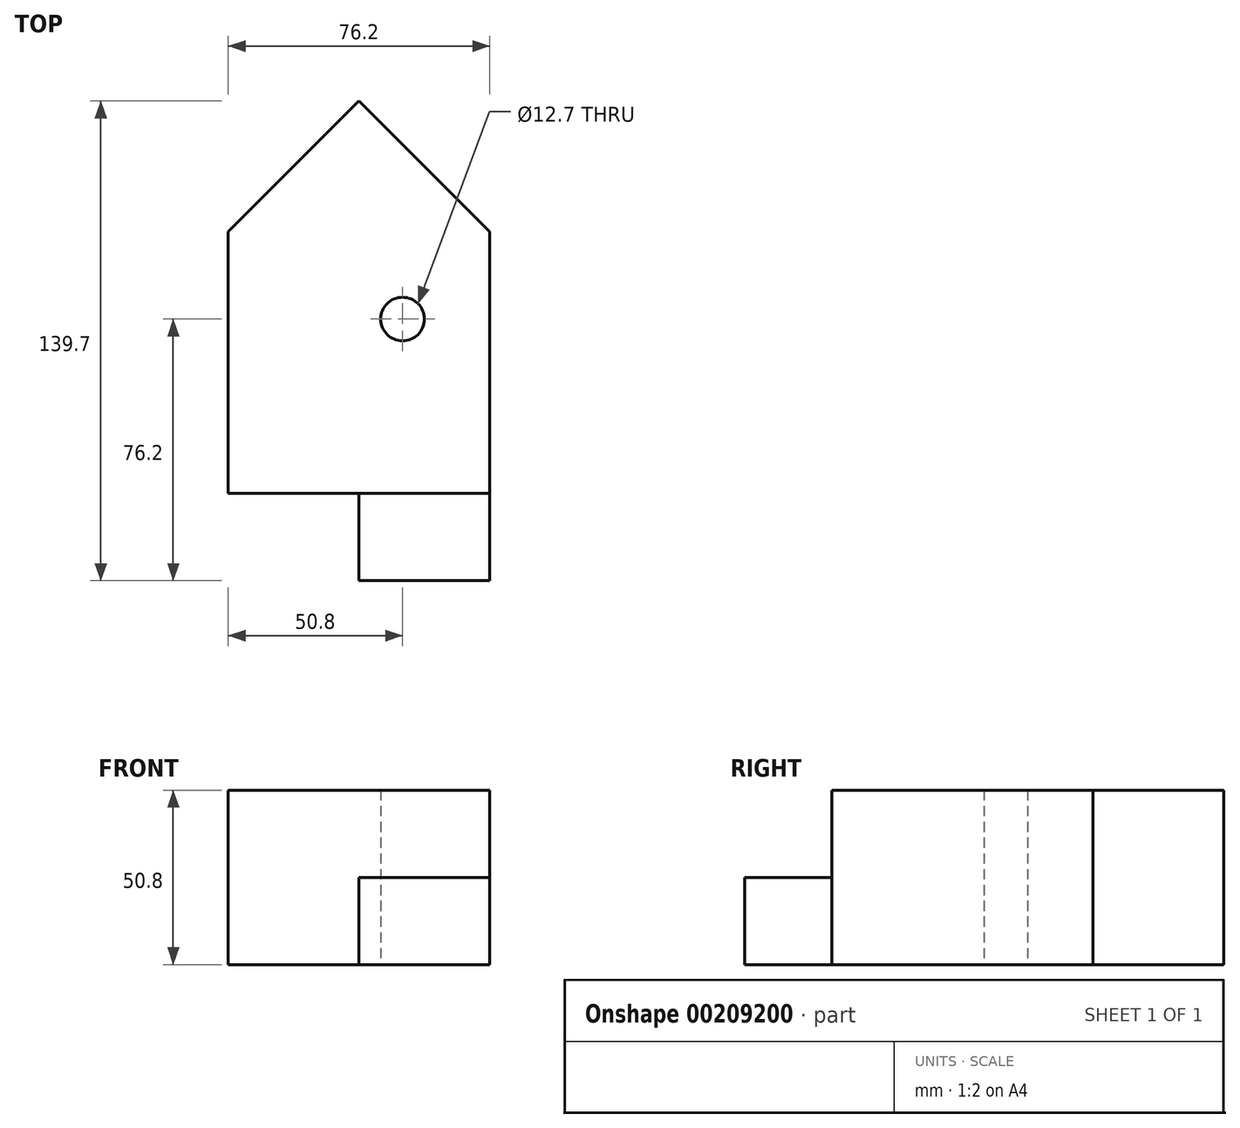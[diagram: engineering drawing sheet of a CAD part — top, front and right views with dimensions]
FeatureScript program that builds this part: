
annotation { "Feature Type Name" : "Feature", "Feature Type Description" : "" }
export const myFeature = defineFeature(function(context is Context, id is Id, definition is map)
    precondition{}
    {
        {
            var Q0;
            Q0=qCreatedBy(makeId("Top.planeOp"),FACE);
            var sketch = newSketch(context, id + "F0", { "sketchPlane" : qUnion([Q0])});
            skLineSegment(sketch, "E0.bottom", {"start": v(0, 0) * mm, "end": v(76.2, 0) * mm});
            skLineSegment(sketch, "E0.top", {"start": v(0, 76.2) * mm, "end": v(76.2, 76.2) * mm});
            skLineSegment(sketch, "E0.left", {"start": v(0, 0) * mm, "end": v(0, 76.2) * mm});
            skLineSegment(sketch, "E0.right", {"start": v(76.2, 0) * mm, "end": v(76.2, 76.2) * mm});
            skLineSegment(sketch, "E1", {"start": v(0, 76.2) * mm, "end": v(38.1, 114.3) * mm});
            skPoint(sketch, "E1.endSnap0", {"position": v(38.1, 76.2) * mm});
            skLineSegment(sketch, "E2", {"start": v(38.1, 114.3) * mm, "end": v(76.2, 76.2) * mm});
            skSolve(sketch);
        }
        {
            var Q0;
            Q0 = qSketchRegion(id + "F0", true);
            extrude(context, id + "F1", {"entities" : qUnion([Q0]), "depth" : 50.8 * mm});
        }
        {
            var Q0;
            Q0=makeQuery(id+"F1.opExtrude","CAP_FACE",FACE,{"disambiguationData":[OSD([sQuery(id+"F0.wireOp",EDGE,"E0.bottom"),sQuery(id+"F0.wireOp",EDGE,"E0.left"),sQuery(id+"F0.wireOp",EDGE,"E0.right"),sQuery(id+"F0.wireOp",EDGE,"E1"),sQuery(id+"F0.wireOp",EDGE,"E2")])],"isStart":true});
            var sketch = newSketch(context, id + "F2", { "sketchPlane" : qUnion([Q0])});
            skCircle(sketch, "E3", {"center": v(50.8, -50.8) * mm, "radius": 6.35 * mm});
            skSolve(sketch);
        }
        {
            var Q0;
            Q0=makeQuery(id+"F2.imprint","IMPRINT",FACE,{"disambiguationData":[TD([[makeQuery(id+"F2.imprint","IMPRINT",EDGE,{"derivedFrom":sQuery(id+"F2.wireOp",EDGE,"E3")}),1.0]])]});
            extrude(context, id + "F3", {"entities" : qUnion([Q0]), "operationType" : NewBodyOperationType.REMOVE, "oppositeDirection" : true, "depth" : 50.8 * mm});
        }
        {
            var Q0;
            Q0=makeQuery(id+"F1.opExtrude","SWEPT_FACE",FACE,{"disambiguationData":[OSD([sQuery(id+"F0.wireOp",EDGE,"E0.bottom")])]});
            var sketch = newSketch(context, id + "F4", { "sketchPlane" : qUnion([Q0])});
            skLineSegment(sketch, "E4.bottom", {"start": v(76.2, 0) * mm, "end": v(38.1, 0) * mm});
            skLineSegment(sketch, "E4.top", {"start": v(76.2, 25.4) * mm, "end": v(38.1, 25.4) * mm});
            skLineSegment(sketch, "E4.left", {"start": v(76.2, 0) * mm, "end": v(76.2, 25.4) * mm});
            skLineSegment(sketch, "E4.right", {"start": v(38.1, 0) * mm, "end": v(38.1, 25.4) * mm});
            skSolve(sketch);
        }
        {
            var Q0;
            Q0 = qSketchRegion(id + "F4", true);
            extrude(context, id + "F5", {"entities" : qUnion([Q0]), "depth" : 25.4 * mm});
        }
    });
